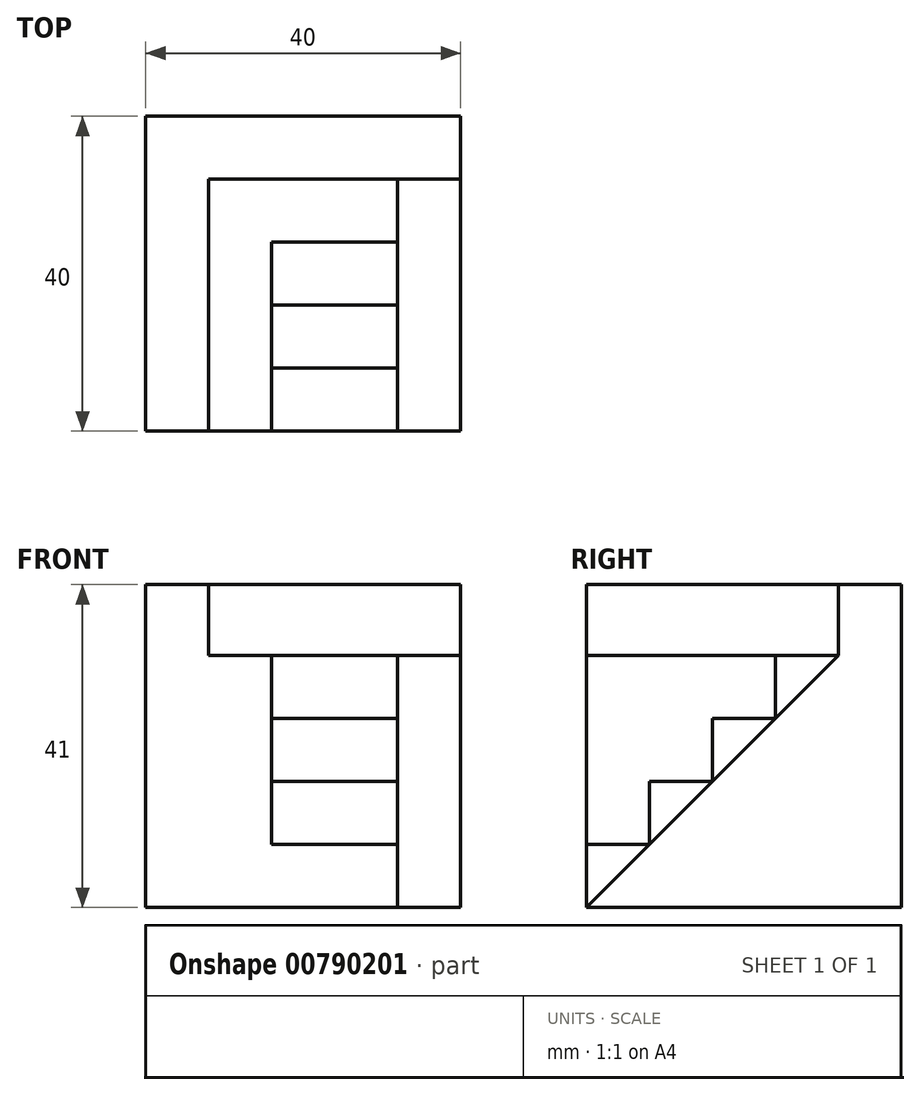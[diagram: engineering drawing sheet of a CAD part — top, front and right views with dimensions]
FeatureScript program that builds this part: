
annotation { "Feature Type Name" : "Feature", "Feature Type Description" : "" }
export const myFeature = defineFeature(function(context is Context, id is Id, definition is map)
    precondition{}
    {
        {
            var Q0;
            Q0=qCreatedBy(makeId("Top.planeOp"),FACE);
            var sketch = newSketch(context, id + "F0", { "sketchPlane" : qUnion([Q0])});
            skLineSegment(sketch, "E0.bottom", {"start": v(-20, 20) * mm, "end": v(20, 20) * mm});
            skLineSegment(sketch, "E0.top", {"start": v(-20, -20) * mm, "end": v(20, -20) * mm});
            skLineSegment(sketch, "E0.left", {"start": v(-20, 20) * mm, "end": v(-20, -20) * mm});
            skLineSegment(sketch, "E0.right", {"start": v(20, 20) * mm, "end": v(20, -20) * mm});
            skPoint(sketch, "E0.middle", {"position": v(0, 0) * mm});
            skLineSegment(sketch, "E1", {"start": v(12, -20) * mm, "end": v(12, 12) * mm});
            skLineSegment(sketch, "E2", {"start": v(20, 12) * mm, "end": v(-12, 12) * mm});
            skLineSegment(sketch, "E3", {"start": v(-4, 4) * mm, "end": v(-4, -20) * mm});
            skLineSegment(sketch, "E4", {"start": v(12, -12) * mm, "end": v(-4, -12) * mm});
            skLineSegment(sketch, "E5", {"start": v(-4, -4) * mm, "end": v(12, -4) * mm});
            skLineSegment(sketch, "E6", {"start": v(-4, 4) * mm, "end": v(12, 4) * mm});
            skLineSegment(sketch, "E7", {"start": v(-12, 12) * mm, "end": v(-12, -20) * mm});
            skPoint(sketch, "E8.orphan", {"position": v(20, 4) * mm});
            skPoint(sketch, "E9.orphan", {"position": v(20, -4) * mm});
            skPoint(sketch, "E10.orphan", {"position": v(20, -12) * mm});
            skPoint(sketch, "E11.orphan", {"position": v(-4, 12) * mm});
            skPoint(sketch, "E12.start.orphan", {"position": v(-12, 20) * mm});
            skSolve(sketch);
        }
        {
            var Q0;
            {var subQ1=sQuery(id+"F0.wireOp",EDGE,"E0.top");var subQ4=sQuery(id+"F0.wireOp",EDGE,"E0.right");var subQ5=makeQuery(id+"F0.imprint","INTERSECT",VERTEX,{"derivedFrom":[subQ1,subQ4]});Q0=makeQuery(id+"F0.imprint","IMPRINT",FACE,{"disambiguationData":[TD([[makeQuery(id+"F0.imprint","IMPRINT",EDGE,{"disambiguationData":[TD([[subQ5,1.0]])],"derivedFrom":subQ1}),1.0]])]});}
            extrude(context, id + "F1", {"entities" : qUnion([Q0]), "depth" : 32 * mm, "offsetDistance" : 25 * mm});
        }
        {
            var Q0;
            Q0=makeQuery(id+"F1.opExtrude","SWEPT_FACE",FACE,{"disambiguationData":[OSD([sQuery(id+"F0.wireOp",EDGE,"E0.right")])]});
            var sketch = newSketch(context, id + "F2", { "sketchPlane" : qUnion([Q0])});
            skLineSegment(sketch, "E13", {"start": v(12, 32) * mm, "end": v(-20, 0) * mm});
            skSolve(sketch);
        }
        {
            var Q0;
            Q0=makeQuery(id+"F2.imprint","IMPRINT",FACE,{"disambiguationData":[TD([[makeQuery(id+"F2.imprint","IMPRINT",EDGE,{"derivedFrom":sQuery(id+"F2.wireOp",EDGE,"E13")}),-1.0]])]});
            extrude(context, id + "F3", {"entities" : qUnion([Q0]), "operationType" : NewBodyOperationType.REMOVE, "oppositeDirection" : true, "depth" : 25 * mm, "offsetDistance" : 25 * mm});
        }
        {
            var Q0;
            {var subQ1=sQuery(id+"F0.wireOp",EDGE,"E0.bottom");Q0=makeQuery(id+"F0.imprint","IMPRINT",FACE,{"disambiguationData":[TD([[makeQuery(id+"F0.imprint","IMPRINT",EDGE,{"derivedFrom":subQ1}),-1.0]])]});}
            extrude(context, id + "F4", {"entities" : qUnion([Q0]), "operationType" : NewBodyOperationType.ADD, "depth" : 41 * mm, "offsetDistance" : 25 * mm});
        }
        {
            var Q0;
            {var subQ0=sQuery(id+"F0.wireOp",EDGE,"E6");Q0=makeQuery(id+"F0.imprint","IMPRINT",FACE,{"disambiguationData":[TD([[makeQuery(id+"F0.imprint","IMPRINT",EDGE,{"derivedFrom":subQ0}),1.0]])]});}
            extrude(context, id + "F5", {"entities" : qUnion([Q0]), "operationType" : NewBodyOperationType.ADD, "depth" : 32 * mm, "offsetDistance" : 25 * mm});
        }
        {
            var Q0;
            {var subQ0=sQuery(id+"F0.wireOp",EDGE,"E5");Q0=makeQuery(id+"F0.imprint","IMPRINT",FACE,{"disambiguationData":[TD([[makeQuery(id+"F0.imprint","IMPRINT",EDGE,{"derivedFrom":subQ0}),1.0]])]});}
            extrude(context, id + "F6", {"entities" : qUnion([Q0]), "operationType" : NewBodyOperationType.ADD, "depth" : 24 * mm, "offsetDistance" : 25 * mm});
        }
        {
            var Q0;
            {var subQ0=sQuery(id+"F0.wireOp",EDGE,"E4");Q0=makeQuery(id+"F0.imprint","IMPRINT",FACE,{"disambiguationData":[TD([[makeQuery(id+"F0.imprint","IMPRINT",EDGE,{"derivedFrom":subQ0}),-1.0]])]});}
            extrude(context, id + "F7", {"entities" : qUnion([Q0]), "operationType" : NewBodyOperationType.ADD, "depth" : 16 * mm, "offsetDistance" : 25 * mm});
        }
        {
            var Q0;
            {var subQ5=sQuery(id+"F0.wireOp",EDGE,"E4");Q0=makeQuery(id+"F0.imprint","IMPRINT",FACE,{"disambiguationData":[TD([[makeQuery(id+"F0.imprint","IMPRINT",EDGE,{"derivedFrom":subQ5}),1.0]])]});}
            extrude(context, id + "F8", {"entities" : qUnion([Q0]), "operationType" : NewBodyOperationType.ADD, "depth" : 8 * mm, "offsetDistance" : 25 * mm});
        }
    });
